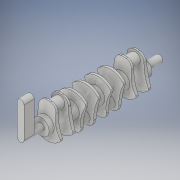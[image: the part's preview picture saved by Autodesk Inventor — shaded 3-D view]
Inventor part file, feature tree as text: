
AUTODESK INVENTOR PART (.ipt)
format: ipt  version: 2018 (Build 220112000, 112)  size: 534,016 bytes
history: native  units: in
note: dims shown in document units (in); Inventor stores cm internally (conversion verified against a paired STEP export)
features: extrude x19, sketch x18, plane x9, projected_geometry x7, loft x4, fillet x4, other x4, mirror x2
ambient origin geometry x8: Origin, YZ Plane, XZ Plane, XY Plane, X Axis, Y Axis, Z Axis, Center Point
bodies: Solid1 (feature_tree)
feature tree (67):
  extrude  "Extrusion1"  Depth=1.0in TaperAngle=0.0deg
  extrude  "Extrusion2"  Depth=1.0in TaperAngle=0.0deg
  plane  "Work Plane1"
  plane  "Work Plane2"
  sketch  "Sketch3"  dims[d6=0.25in d7=0.5in]
  loft  "Loft1"
  extrude  "Extrusion3"  TaperAngle=0.0deg  [1 undecoded]
  extrude  "Extrusion4"  Depth=0.25in TaperAngle=0.0deg
  extrude  "Extrusion5"  Depth=1.5in
  plane  "Work Plane3"
  sketch  "Sketch6"  dims[d15=1.5in d16=1.85in]
  loft  "Loft2"
  extrude  "Extrusion6"  TaperAngle=0.0deg  [1 undecoded]
  plane  "Work Plane4"
  sketch  "Sketch7"  dims[d17=1.5in d18=0.0in d19=0.25in d20=0.0in]
  loft  "Loft3"
  extrude  "Extrusion7"  Depth=0.25in
  extrude  "Extrusion8"  TaperAngle=0.0deg  [1 undecoded]
  extrude  "Extrusion9"  Depth=1.5in
  fillet  "Fillet1"  Radius=1.85in
  extrude  "Extrusion10"  Depth=4.5in TaperAngle=0.0deg
  plane  "Work Plane5"
  loft  "Loft4"
  extrude  "Extrusion11"  Depth=0.3138in
  extrude  "Extrusion12"  Depth=0.25in TaperAngle=0.0deg
  fillet  "Fillet2"  Radius=0.25in
  fillet  "Fillet3"  [1 undecoded]
  mirror  "Mirror1"
  extrude  "Extrusion13"  Depth=0.6in TaperAngle=0.0deg
  plane  "Work Plane8"
  mirror  "Mirror2"
  extrude  "Extrusion14"  Depth=0.5in
  plane  "Work Plane9"
  sketch  "Sketch16"  dims[d44=6.0in d45=0.3138in]
  extrude  "Extrusion15"  Depth=0.5in
  extrude  "Extrusion16"  Depth=0.5in
  extrude  "Extrusion17"  Depth=0.5in
  extrude  "Extrusion18"  Depth=0.5in
  extrude  "Extrusion19"  TaperAngle=0.0deg  [1 undecoded]
  fillet  "Fillet4"  Radius=3.0in
  sketch  "Sketch1"  dims[d0=1.0in d1=2.0in d2=0.0in]
  sketch  "Sketch2"  dims[d3=2.36in d4=1.0in d5=0.0in]
  other  "Edges1"
  sketch  "Sketch4"  dims[d8=5.7in d9=0.0in d10=90.0deg]
  sketch  "Sketch5"  dims[d11=0.0in d12=90.0deg d13=0.25in d14=0.0in]
  other  "Edges2"
  other  "Edges3"
  sketch  "Sketch8"  dims[d21=0.25in d22=0.0in d23=90.0deg]
  projected_geometry  "Projected Loop1"
  sketch  "Sketch10"  dims[d24=0.0in d25=90.0deg d26=1.2in d27=0.0in]
  sketch  "Sketch11"  dims[d28=0.25in d29=5.7in]
  projected_geometry  "Projected Loop2"
  other  "Edges4"
  sketch  "Sketch12"  dims[d30=0.0in d31=90.0deg d32=0.0in d33=90.0deg]
  projected_geometry  "Projected Loop3"
  sketch  "Sketch13"  dims[d34=0.25in d35=0.0in d36=1.5in d37=1.85in]
  projected_geometry  "Projected Loop4"
  plane  "Work Plane6"
  plane  "Work Plane7"
  sketch  "Sketch14"  dims[d38=1.5in d39=0.0in d40=4.5in d41=0.0in]
  projected_geometry  "Projected Loop5"
  sketch  "Sketch15"  dims[d42=1.3in d43=6.5in]
  projected_geometry  "Projected Loop6"
  sketch  "Sketch17"  dims[d46=1.0in d47=0.25in d48=0.0in d49=0.25in d50=0.0in d51=90.0deg]
  sketch  "Sketch18"  dims[d52=0.0in d53=90.0deg d54=0.6in d55=0.0in]
  sketch  "Sketch19"  dims[d56=6.5in d57=0.314in d58=6.0in d59=3.4in d60=3.4in d61=3.4in d62=0.0in d63=3.0in d64=0.0in d65=1.0in d66=0.25in d67=0.25in d68=0.0in d69=0.0in d70=2.5in d71=0.25in d72=0.25in d73=0.25in d74=4.0in d75=0.0in d76=0.0in d77=2.5in d78=0.25in d79=0.25in d80=5.0in d81=0.0in d82=2.0in d83=0.0in d84=180.0deg d85=2.5in d86=0.25in d87=0.25in d88=4.0in d89=0.0in d90=5.0in d91=1.5in d92=0.0in d93=1.5in d94=0.0in d98=0.5in]
  projected_geometry  "Projected Loop7"
note: 5 required parameter values undecoded (feature->parameter linkage not recoverable at this tier; creation-order binding heuristic only, values carry confidence <= 0.55)
